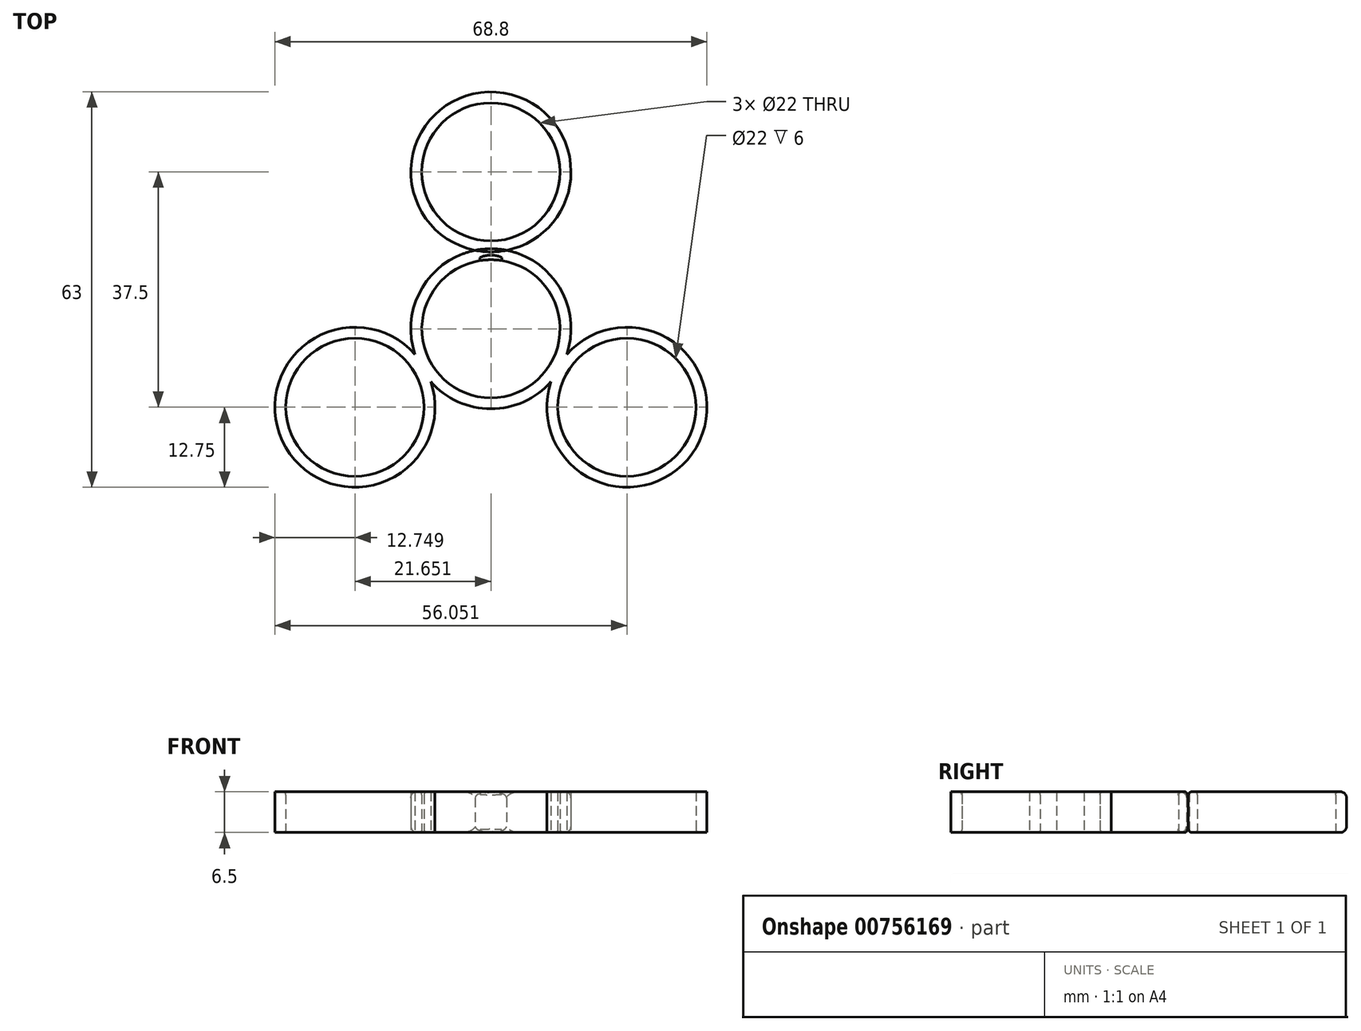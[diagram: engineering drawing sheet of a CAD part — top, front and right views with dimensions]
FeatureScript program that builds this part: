
annotation { "Feature Type Name" : "Feature", "Feature Type Description" : "" }
export const myFeature = defineFeature(function(context is Context, id is Id, definition is map)
    precondition{}
    {
        {
            var Q0;
            Q0=qCreatedBy(makeId("Top.planeOp"),FACE);
            var sketch = newSketch(context, id + "F0", { "sketchPlane" : qUnion([Q0])});
            skCircle(sketch, "E0", {"center": v(0, 0) * mm, "radius": 11 * mm});
            skCircle(sketch, "E1", {"center": v(0, 0) * mm, "radius": 12.75 * mm});
            skLineSegment(sketch, "E2", {"start": v(0, 0) * mm, "end": v(0, 25) * mm, "construction": true});
            skLineSegment(sketch, "E3", {"start": v(0, 0) * mm, "end": v(-21.65, -12.5) * mm, "construction": true});
            skLineSegment(sketch, "E4", {"start": v(0, 0) * mm, "end": v(21.65, -12.5) * mm, "construction": true});
            skCircle(sketch, "E5", {"center": v(0, 25) * mm, "radius": 11 * mm});
            skCircle(sketch, "E6", {"center": v(21.65, -12.5) * mm, "radius": 11 * mm});
            skCircle(sketch, "E7", {"center": v(-21.65, -12.5) * mm, "radius": 11 * mm});
            skCircle(sketch, "E8", {"center": v(0, 25) * mm, "radius": 12.75 * mm});
            skCircle(sketch, "E9", {"center": v(21.65, -12.5) * mm, "radius": 12.75 * mm});
            skCircle(sketch, "E10", {"center": v(-21.65, -12.5) * mm, "radius": 12.75 * mm});
            skLineSegment(sketch, "E11", {"start": v(0, 0) * mm, "end": v(23.38, 13.5) * mm, "construction": true});
            skLineSegment(sketch, "E12", {"start": v(0, 0) * mm, "end": v(0, -27) * mm, "construction": true});
            skLineSegment(sketch, "E13", {"start": v(0, 0) * mm, "end": v(-23.38, 13.5) * mm, "construction": true});
            skCircle(sketch, "E14", {"center": v(-23.38, 13.5) * mm, "radius": 13.3 * mm});
            skCircle(sketch, "E15", {"center": v(23.38, 13.5) * mm, "radius": 13.3 * mm});
            skCircle(sketch, "E16", {"center": v(0, -27) * mm, "radius": 13.3 * mm});
            skSolve(sketch);
        }
        {
            var Q0;
            Q0=makeQuery(id+"F0.imprint","IMPRINT",FACE,{"disambiguationData":[TD([[makeQuery(id+"F0.imprint","IMPRINT",EDGE,{"derivedFrom":sQuery(id+"F0.wireOp",EDGE,"E5")}),-1.0]])]});
            var Q1;
            {var subQ0=sQuery(id+"F0.wireOp",EDGE,"E14");var subQ1=makeQuery(id+"F0.imprint","IMPRINT",VERTEX,{"derivedFrom":subQ0});Q1=makeQuery(id+"F0.imprint","IMPRINT",FACE,{"disambiguationData":[TD([[makeQuery(id+"F0.imprint","IMPRINT",EDGE,{"disambiguationData":[TD([[subQ1,-1.0]])],"derivedFrom":subQ0}),-1.0]])]});}
            var Q2;
            {var subQ3=sQuery(id+"F0.wireOp",EDGE,"E1");var subQ8=makeQuery(id+"F0.imprint","IMPRINT",VERTEX,{"derivedFrom":subQ3});Q2=makeQuery(id+"F0.imprint","IMPRINT",FACE,{"disambiguationData":[TD([[makeQuery(id+"F0.imprint","IMPRINT",EDGE,{"disambiguationData":[TD([[subQ8,-1.0]])],"derivedFrom":subQ3}),-1.0]])]});}
            var Q3;
            Q3=makeQuery(id+"F0.imprint","IMPRINT",FACE,{"disambiguationData":[TD([[makeQuery(id+"F0.imprint","IMPRINT",EDGE,{"derivedFrom":sQuery(id+"F0.wireOp",EDGE,"E6")}),-1.0]])]});
            var Q4;
            {var subQ0=sQuery(id+"F0.wireOp",EDGE,"E10");var subQ1=makeQuery(id+"F0.imprint","IMPRINT",VERTEX,{"derivedFrom":subQ0});Q4=makeQuery(id+"F0.imprint","IMPRINT",FACE,{"disambiguationData":[TD([[makeQuery(id+"F0.imprint","IMPRINT",EDGE,{"disambiguationData":[TD([[subQ1,-1.0]])],"derivedFrom":subQ0}),-1.0]])]});}
            var Q5;
            Q5=makeQuery(id+"F0.imprint","IMPRINT",FACE,{"disambiguationData":[TD([[makeQuery(id+"F0.imprint","IMPRINT",EDGE,{"derivedFrom":sQuery(id+"F0.wireOp",EDGE,"E7")}),-1.0]])]});
            var Q6;
            {var subQ0=sQuery(id+"F0.wireOp",EDGE,"E10");var subQ1=sQuery(id+"F0.wireOp",EDGE,"E1");var subQ2=makeQuery(id+"F0.imprint","INTERSECT",VERTEX,{"disambiguationData":[OD(0.0)],"derivedFrom":[subQ1,subQ0]});Q6=makeQuery(id+"F0.imprint","IMPRINT",FACE,{"disambiguationData":[TD([[makeQuery(id+"F0.imprint","IMPRINT",EDGE,{"disambiguationData":[TD([[subQ2,-1.0]])],"derivedFrom":subQ1}),1.0]])]});}
            var Q7;
            Q7=makeQuery(id+"F0.imprint","IMPRINT",FACE,{"disambiguationData":[TD([[makeQuery(id+"F0.imprint","IMPRINT",EDGE,{"derivedFrom":sQuery(id+"F0.wireOp",EDGE,"E0")}),-1.0]])]});
            var Q8;
            {var subQ0=sQuery(id+"F0.wireOp",EDGE,"E9");var subQ1=sQuery(id+"F0.wireOp",EDGE,"E1");var subQ2=makeQuery(id+"F0.imprint","INTERSECT",VERTEX,{"disambiguationData":[OD(0.0)],"derivedFrom":[subQ1,subQ0]});Q8=makeQuery(id+"F0.imprint","IMPRINT",FACE,{"disambiguationData":[TD([[makeQuery(id+"F0.imprint","IMPRINT",EDGE,{"disambiguationData":[TD([[subQ2,-1.0]])],"derivedFrom":subQ1}),1.0]])]});}
            var Q9;
            {var subQ0=sQuery(id+"F0.wireOp",EDGE,"E8");var subQ1=sQuery(id+"F0.wireOp",EDGE,"E1");var subQ2=makeQuery(id+"F0.imprint","INTERSECT",VERTEX,{"disambiguationData":[OD(0.0)],"derivedFrom":[subQ1,subQ0]});Q9=makeQuery(id+"F0.imprint","IMPRINT",FACE,{"disambiguationData":[TD([[makeQuery(id+"F0.imprint","IMPRINT",EDGE,{"disambiguationData":[TD([[subQ2,-1.0]])],"derivedFrom":subQ1}),1.0]])]});}
            extrude(context, id + "F1", {"entities" : qUnion([Q0, Q1, Q2, Q3, Q4, Q5, Q6, Q7, Q8, Q9]), "depth" : 6.5 * mm, "offsetDistance" : 25 * mm});
        }
        {
            var Q0;
            Q0=makeQuery(id+"F1.opExtrude","CAP_EDGE",EDGE,{"disambiguationData":[OSD([sQuery(id+"F0.wireOp",EDGE,"E8")])],"isStart":false});
            var Q1;
            Q1=makeQuery(id+"F1.opExtrude","CAP_EDGE",EDGE,{"disambiguationData":[OSD([sQuery(id+"F0.wireOp",EDGE,"E8")])],"isStart":true});
            fillet(context, id + "F2", {"entities" : qUnion([Q0, Q1]), "tangentPropagation" : true, "radius" : 1 * mm, "defaultsChanged" : true, "vertexSettings" : [], "allowEdgeOverflow" : false});
        }
        {
            var Q0;
            Q0=makeQuery(id+"F1.opExtrude","CAP_EDGE",EDGE,{"disambiguationData":[OSD([sQuery(id+"F0.wireOp",EDGE,"E5")])],"isStart":false});
            var Q1;
            Q1=makeQuery(id+"F1.opExtrude","CAP_EDGE",EDGE,{"disambiguationData":[OSD([sQuery(id+"F0.wireOp",EDGE,"E0")])],"isStart":false});
            var Q2;
            Q2=makeQuery(id+"F1.opExtrude","CAP_EDGE",EDGE,{"disambiguationData":[OSD([sQuery(id+"F0.wireOp",EDGE,"E7")])],"isStart":false});
            var Q3;
            Q3=makeQuery(id+"F1.opExtrude","CAP_EDGE",EDGE,{"disambiguationData":[OSD([sQuery(id+"F0.wireOp",EDGE,"E5")])],"isStart":true});
            var Q4;
            Q4=makeQuery(id+"F1.opExtrude","CAP_EDGE",EDGE,{"disambiguationData":[OSD([sQuery(id+"F0.wireOp",EDGE,"E0")])],"isStart":true});
            var Q5;
            Q5=makeQuery(id+"F1.opExtrude","CAP_EDGE",EDGE,{"disambiguationData":[OSD([sQuery(id+"F0.wireOp",EDGE,"E7")])],"isStart":true});
            var Q6;
            Q6=makeQuery(id+"F1.opExtrude","CAP_EDGE",EDGE,{"disambiguationData":[OSD([sQuery(id+"F0.wireOp",EDGE,"E6")])],"isStart":true});
            fillet(context, id + "F3", {"entities" : qUnion([Q0, Q1, Q2, Q3, Q4, Q5, Q6]), "tangentPropagation" : true, "radius" : 0.5 * mm, "defaultsChanged" : false, "vertexSettings" : [], "allowEdgeOverflow" : false});
        }
    });
